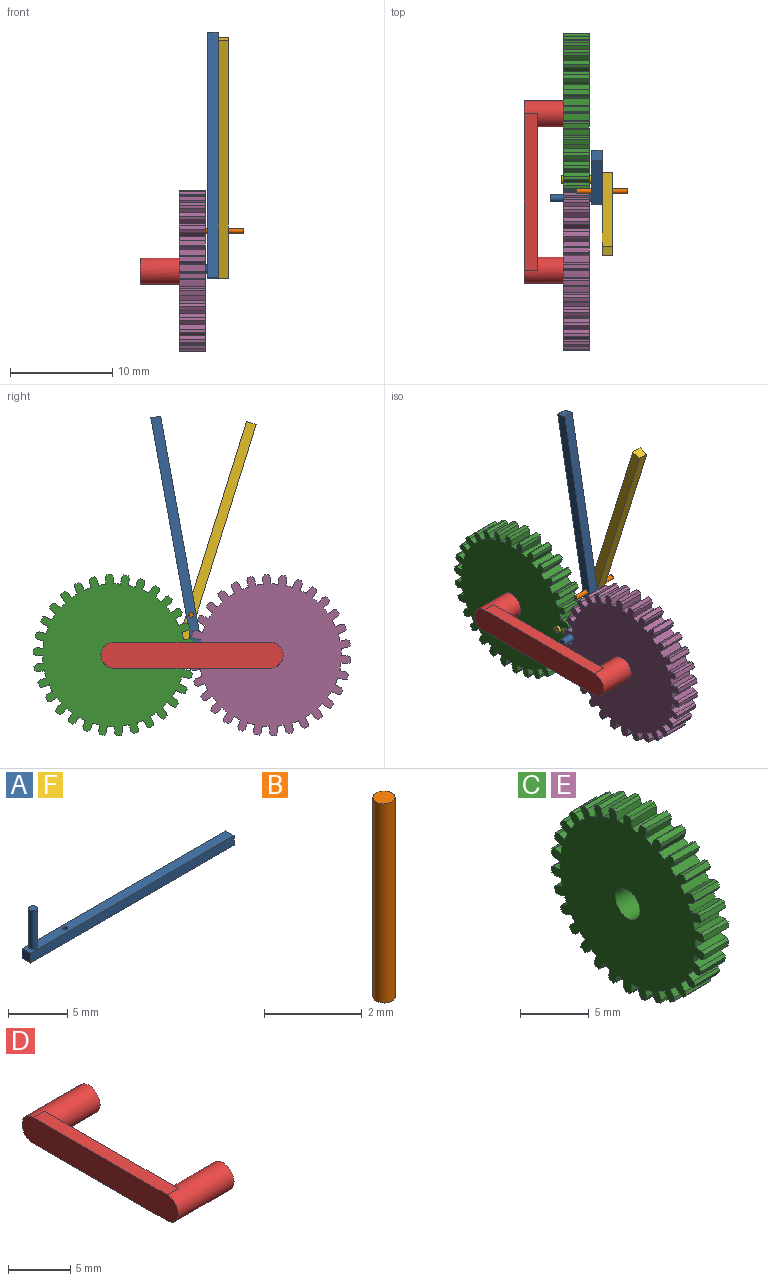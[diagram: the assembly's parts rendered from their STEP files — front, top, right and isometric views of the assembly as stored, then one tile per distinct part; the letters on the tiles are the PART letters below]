
ASSEMBLY  parts=6 mates=4
PART A: 9 faces, bbox 24.3x1x5 mm
  f0: plane 24.3x1mm, normal (0,1,0), area 24.3mm2, adj f1,f4,f5,f6
  f1: plane 1x0.98mm, normal (-1,0,0), area 1mm2, adj f0,f2,f5,f6
  f2: plane 24.3x1mm, normal (0,-1,0), area 24.3mm2, adj f1,f4,f5,f6
  f3: cylinder r=0.23mm len=1mm, axis (0,0,-1), area 1.4mm2, adj f5,f6
  f4: plane 1x0.98mm, normal (1,0,0), area 1mm2, adj f0,f2,f5,f6
  f5: plane 24.3x0.98mm, normal (0,0,1), area 23.3mm2, adj f0,f1,f2,f3,f4,f7
  f6: plane 24.3x0.98mm, normal (0,0,-1), area 23.7mm2, adj f0,f1,f2,f3,f4
  f7: cylinder r=0.36mm len=4mm, axis (0,0,-1), area 9.1mm2, adj f5,f8
  f8: plane 0.73x0.73mm, normal (0,0,1), area 0.4mm2, adj f7
PART B: 3 faces, bbox 0.5x0.5x5 mm
  f0: cylinder r=0.23mm len=5mm, axis (0,0,1), area 7.1mm2, adj f1,f2
  f1: plane 0.45x0.45mm, normal (0,0,-1), area 0.2mm2, adj f0
  f2: plane 0.45x0.45mm, normal (0,0,1), area 0.2mm2, adj f0
PART C: 183 faces, bbox 2.5x15.7x15.8 mm
  f0: cylinder r=6.97mm len=2.54mm, axis (1,0,0), area 1.8mm2, adj f29,f30,f34,f178
  f1: cylinder r=6.97mm len=2.54mm, axis (1,0,0), area 1.8mm2, adj f29,f30,f41,f175
  f2: cylinder r=6.97mm len=2.54mm, axis (1,0,0), area 1.8mm2, adj f29,f30,f46,f170
  f3: cylinder r=6.97mm len=2.54mm, axis (1,0,0), area 1.8mm2, adj f29,f30,f51,f165
  f4: cylinder r=6.97mm len=2.54mm, axis (1,0,0), area 1.8mm2, adj f29,f30,f56,f160
  f5: cylinder r=6.97mm len=2.54mm, axis (1,0,0), area 1.8mm2, adj f29,f30,f61,f155
  f6: cylinder r=6.97mm len=2.54mm, axis (1,0,0), area 1.8mm2, adj f29,f30,f64,f150
  f7: cylinder r=6.97mm len=2.54mm, axis (1,0,0), area 1.8mm2, adj f29,f30,f145,f151
  f8: cylinder r=6.97mm len=2.54mm, axis (1,0,0), area 1.8mm2, adj f29,f30,f140,f146
  f9: cylinder r=6.97mm len=2.54mm, axis (1,0,0), area 1.8mm2, adj f29,f30,f135,f141
  f10: cylinder r=6.97mm len=2.54mm, axis (1,0,0), area 1.8mm2, adj f29,f30,f130,f136
  f11: cylinder r=6.97mm len=2.54mm, axis (1,0,0), area 1.8mm2, adj f29,f30,f125,f131
  f12: cylinder r=6.97mm len=2.54mm, axis (1,0,0), area 1.8mm2, adj f29,f30,f120,f126
  f13: cylinder r=6.97mm len=2.54mm, axis (1,0,0), area 1.8mm2, adj f29,f30,f115,f121
  f14: cylinder r=6.97mm len=2.54mm, axis (1,0,0), area 1.8mm2, adj f29,f30,f110,f116
  f15: cylinder r=6.97mm len=2.54mm, axis (1,0,0), area 1.8mm2, adj f29,f30,f105,f111
  f16: cylinder r=6.97mm len=2.54mm, axis (1,0,0), area 1.8mm2, adj f29,f30,f100,f106
  f17: cylinder r=6.97mm len=2.54mm, axis (1,0,0), area 1.8mm2, adj f29,f30,f95,f101
  f18: cylinder r=6.97mm len=2.54mm, axis (1,0,0), area 1.8mm2, adj f29,f30,f90,f96
  f19: cylinder r=6.97mm len=2.54mm, axis (1,0,0), area 1.8mm2, adj f29,f30,f85,f91
  f20: cylinder r=6.97mm len=2.54mm, axis (1,0,0), area 1.8mm2, adj f29,f30,f80,f86
  f21: cylinder r=6.97mm len=2.54mm, axis (1,0,0), area 1.8mm2, adj f29,f30,f75,f156
  f22: cylinder r=6.97mm len=2.54mm, axis (1,0,0), area 1.8mm2, adj f29,f30,f70,f76
  f23: cylinder r=6.97mm len=2.54mm, axis (1,0,0), area 1.8mm2, adj f29,f30,f65,f71
  f24: cylinder r=6.97mm len=2.54mm, axis (1,0,0), area 1.8mm2, adj f29,f30,f60,f161
  f25: cylinder r=6.97mm len=2.54mm, axis (1,0,0), area 1.8mm2, adj f29,f30,f55,f166
  f26: cylinder r=6.97mm len=2.54mm, axis (1,0,0), area 1.8mm2, adj f29,f30,f50,f171
  f27: cylinder r=6.97mm len=2.54mm, axis (1,0,0), area 1.8mm2, adj f29,f30,f45,f176
  f28: cylinder r=6.97mm len=2.54mm, axis (1,0,0), area 1.8mm2, adj f29,f30,f40,f179
  f29: plane 15.76x15.72mm, normal (1,0,0), area 167.1mm2, adj f0,f1,f2,f3,f4,f5,f6,f7
  f30: plane 15.76x15.72mm, normal (-1,0,0), area 167.1mm2, adj f0,f1,f2,f3,f4,f5,f6,f7
  f31: cylinder r=7.88mm len=2.54mm, axis (-1,0,0), area 1.2mm2, adj f29,f30,f35,f36
  f32: plane 2.54x0.66mm, normal (0,1,0), area 1.7mm2, adj f29,f30,f33,f36
  f33: cylinder r=6.97mm len=2.54mm, axis (1,0,0), area 1.8mm2, adj f29,f30,f32,f81
  f34: plane 2.54x0.66mm, normal (0,-1,0), area 1.7mm2, adj f0,f29,f30,f35
  f35: plane 2.54x0.27mm, normal (0,-0.87,0.48), area 0.8mm2, adj f29,f30,f31,f34
  f36: plane 2.54x0.27mm, normal (0,0.87,0.48), area 0.8mm2, adj f29,f30,f31,f32
  f37: cylinder r=7.88mm len=2.54mm, axis (-1,0,0), area 1.2mm2, adj f29,f30,f38,f39
  f38: plane 2.54x0.24mm, normal (0,0.6,0.8), area 0.8mm2, adj f29,f30,f37,f40
  f39: plane 2.54x0.3mm, normal (0,-1,0.09), area 0.8mm2, adj f29,f30,f37,f41
  f40: plane 2.54x0.6mm, normal (0,0.91,0.41), area 1.7mm2, adj f28,f29,f30,f38
  f41: plane 2.54x0.6mm, normal (0,-0.91,-0.41), area 1.7mm2, adj f1,f29,f30,f39
  f42: cylinder r=7.88mm len=2.54mm, axis (-1,0,0), area 1.2mm2, adj f29,f30,f43,f44
  f43: plane 2.54x0.3mm, normal (0,0.22,0.97), area 0.8mm2, adj f29,f30,f42,f45
  f44: plane 2.54x0.29mm, normal (0,-0.95,-0.33), area 0.8mm2, adj f29,f30,f42,f46
  f45: plane 2.54x0.49mm, normal (0,0.67,0.74), area 1.7mm2, adj f27,f29,f30,f43
  f46: plane 2.54x0.49mm, normal (0,-0.67,-0.74), area 1.7mm2, adj f2,f29,f30,f44
  f47: cylinder r=7.88mm len=2.54mm, axis (-1,0,0), area 1.2mm2, adj f29,f30,f48,f49
  f48: plane 2.54x0.3mm, normal (0,-0.19,0.98), area 0.8mm2, adj f29,f30,f47,f50
  f49: plane 2.54x0.22mm, normal (0,-0.73,-0.68), area 0.8mm2, adj f29,f30,f47,f51
  f50: plane 2.54x0.62mm, normal (0,0.31,0.95), area 1.7mm2, adj f26,f29,f30,f48
  f51: plane 2.54x0.62mm, normal (0,-0.31,-0.95), area 1.7mm2, adj f3,f29,f30,f49
  f52: cylinder r=7.88mm len=2.54mm, axis (-1,0,0), area 1.2mm2, adj f29,f30,f53,f54
  f53: plane 2.54x0.25mm, normal (0,-0.57,0.82), area 0.8mm2, adj f29,f30,f52,f55
  f54: plane 2.54x0.28mm, normal (0,-0.39,-0.92), area 0.8mm2, adj f29,f30,f52,f56
  f55: plane 2.54x0.65mm, normal (0,-0.1,0.99), area 1.7mm2, adj f25,f29,f30,f53
  f56: plane 2.54x0.65mm, normal (0,0.1,-0.99), area 1.7mm2, adj f4,f29,f30,f54
  f57: cylinder r=7.88mm len=2.54mm, axis (-1,0,0), area 1.2mm2, adj f29,f30,f58,f59
  f58: plane 2.54x0.26mm, normal (0,-0.86,0.52), area 0.8mm2, adj f29,f30,f57,f60
  f59: plane 2.54x0.31mm, normal (0,0.02,-1), area 0.8mm2, adj f29,f30,f57,f61
  f60: plane 2.54x0.57mm, normal (0,-0.5,0.87), area 1.7mm2, adj f24,f29,f30,f58
  f61: plane 2.54x0.57mm, normal (0,0.5,-0.87), area 1.7mm2, adj f5,f29,f30,f59
  f62: plane 2.54x0.29mm, normal (0,-0.96,-0.29), area 0.8mm2, adj f29,f30,f65,f66
  f63: plane 2.54x0.23mm, normal (0,0.75,-0.66), area 0.8mm2, adj f29,f30,f64,f66
  f64: plane 2.54x0.64mm, normal (0,0.98,-0.21), area 1.7mm2, adj f6,f29,f30,f63
  f65: plane 2.54x0.64mm, normal (0,-0.98,0.21), area 1.7mm2, adj f23,f29,f30,f62
  f66: cylinder r=7.88mm len=2.54mm, axis (-1,0,0), area 1.2mm2, adj f29,f30,f62,f63
  f67: cylinder r=7.88mm len=2.54mm, axis (-1,0,0), area 1.2mm2, adj f29,f30,f68,f69
  f68: plane 2.54x0.3mm, normal (0,-1,-0.09), area 0.8mm2, adj f29,f30,f67,f70
  f69: plane 2.54x0.24mm, normal (0,0.6,-0.8), area 0.8mm2, adj f29,f30,f67,f71
  f70: plane 2.54x0.6mm, normal (0,-0.91,0.41), area 1.7mm2, adj f22,f29,f30,f68
  f71: plane 2.54x0.6mm, normal (0,0.91,-0.41), area 1.7mm2, adj f23,f29,f30,f69
  f72: cylinder r=7.88mm len=2.54mm, axis (-1,0,0), area 1.2mm2, adj f29,f30,f73,f74
  f73: plane 2.54x0.3mm, normal (0,-0.99,0.12), area 0.8mm2, adj f29,f30,f72,f75
  f74: plane 2.54x0.28mm, normal (0,0.42,-0.91), area 0.8mm2, adj f29,f30,f72,f76
  f75: plane 2.54x0.53mm, normal (0,-0.81,0.59), area 1.7mm2, adj f21,f29,f30,f73
  f76: plane 2.54x0.53mm, normal (0,0.81,-0.59), area 1.7mm2, adj f22,f29,f30,f74
  f77: cylinder r=7.88mm len=2.54mm, axis (-1,0,0), area 1.2mm2, adj f29,f30,f78,f79
  f78: plane 2.54x0.29mm, normal (0,0.96,0.29), area 0.8mm2, adj f29,f30,f77,f80
  f79: plane 2.54x0.23mm, normal (0,-0.75,0.66), area 0.8mm2, adj f29,f30,f77,f81
  f80: plane 2.54x0.64mm, normal (0,0.98,-0.21), area 1.7mm2, adj f20,f29,f30,f78
  f81: plane 2.54x0.64mm, normal (0,-0.98,0.21), area 1.7mm2, adj f29,f30,f33,f79
  f82: cylinder r=7.88mm len=2.54mm, axis (-1,0,0), area 1.2mm2, adj f29,f30,f83,f84
  f83: plane 2.54x0.3mm, normal (0,1,0.09), area 0.8mm2, adj f29,f30,f82,f85
  f84: plane 2.54x0.24mm, normal (0,-0.6,0.8), area 0.8mm2, adj f29,f30,f82,f86
  f85: plane 2.54x0.6mm, normal (0,0.91,-0.41), area 1.7mm2, adj f19,f29,f30,f83
  f86: plane 2.54x0.6mm, normal (0,-0.91,0.41), area 1.7mm2, adj f20,f29,f30,f84
  f87: cylinder r=7.88mm len=2.54mm, axis (-1,0,0), area 1.2mm2, adj f29,f30,f88,f89
  f88: plane 2.54x0.3mm, normal (0,0.99,-0.12), area 0.8mm2, adj f29,f30,f87,f90
  f89: plane 2.54x0.28mm, normal (0,-0.42,0.91), area 0.8mm2, adj f29,f30,f87,f91
  f90: plane 2.54x0.53mm, normal (0,0.81,-0.59), area 1.7mm2, adj f18,f29,f30,f88
  f91: plane 2.54x0.53mm, normal (0,-0.81,0.59), area 1.7mm2, adj f19,f29,f30,f89
  f92: cylinder r=7.88mm len=2.54mm, axis (-1,0,0), area 1.2mm2, adj f29,f30,f93,f94
  f93: plane 2.54x0.29mm, normal (0,0.95,-0.33), area 0.8mm2, adj f29,f30,f92,f95
  f94: plane 2.54x0.3mm, normal (0,-0.22,0.97), area 0.8mm2, adj f29,f30,f92,f96
  f95: plane 2.54x0.49mm, normal (0,0.67,-0.74), area 1.7mm2, adj f17,f29,f30,f93
  f96: plane 2.54x0.49mm, normal (0,-0.67,0.74), area 1.7mm2, adj f18,f29,f30,f94
  f97: cylinder r=7.88mm len=2.54mm, axis (-1,0,0), area 1.2mm2, adj f29,f30,f98,f99
  f98: plane 2.54x0.26mm, normal (0,0.86,-0.52), area 0.8mm2, adj f29,f30,f97,f100
  f99: plane 2.54x0.31mm, normal (0,-0.02,1), area 0.8mm2, adj f29,f30,f97,f101
  f100: plane 2.54x0.57mm, normal (0,0.5,-0.87), area 1.7mm2, adj f16,f29,f30,f98
  f101: plane 2.54x0.57mm, normal (0,-0.5,0.87), area 1.7mm2, adj f17,f29,f30,f99
  f102: cylinder r=7.88mm len=2.54mm, axis (-1,0,0), area 1.2mm2, adj f29,f30,f103,f104
  f103: plane 2.54x0.22mm, normal (0,0.73,-0.68), area 0.8mm2, adj f29,f30,f102,f105
  f104: plane 2.54x0.3mm, normal (0,0.19,0.98), area 0.8mm2, adj f29,f30,f102,f106
  f105: plane 2.54x0.62mm, normal (0,0.31,-0.95), area 1.7mm2, adj f15,f29,f30,f103
  f106: plane 2.54x0.62mm, normal (0,-0.31,0.95), area 1.7mm2, adj f16,f29,f30,f104
  f107: cylinder r=7.88mm len=2.54mm, axis (-1,0,0), area 1.2mm2, adj f29,f30,f108,f109
  f108: plane 2.54x0.25mm, normal (0,0.57,-0.82), area 0.8mm2, adj f29,f30,f107,f110
  f109: plane 2.54x0.28mm, normal (0,0.39,0.92), area 0.8mm2, adj f29,f30,f107,f111
  f110: plane 2.54x0.65mm, normal (0,0.1,-0.99), area 1.7mm2, adj f14,f29,f30,f108
  f111: plane 2.54x0.65mm, normal (0,-0.1,0.99), area 1.7mm2, adj f15,f29,f30,f109
  f112: cylinder r=7.88mm len=2.54mm, axis (-1,0,0), area 1.2mm2, adj f29,f30,f113,f114
  f113: plane 2.54x0.28mm, normal (0,0.39,-0.92), area 0.8mm2, adj f29,f30,f112,f115
  f114: plane 2.54x0.25mm, normal (0,0.57,0.82), area 0.8mm2, adj f29,f30,f112,f116
  f115: plane 2.54x0.65mm, normal (0,-0.1,-0.99), area 1.7mm2, adj f13,f29,f30,f113
  f116: plane 2.54x0.65mm, normal (0,0.1,0.99), area 1.7mm2, adj f14,f29,f30,f114
  f117: cylinder r=7.88mm len=2.54mm, axis (-1,0,0), area 1.2mm2, adj f29,f30,f118,f119
  f118: plane 2.54x0.3mm, normal (0,0.19,-0.98), area 0.8mm2, adj f29,f30,f117,f120
  f119: plane 2.54x0.22mm, normal (0,0.73,0.68), area 0.8mm2, adj f29,f30,f117,f121
  f120: plane 2.54x0.62mm, normal (0,-0.31,-0.95), area 1.7mm2, adj f12,f29,f30,f118
  f121: plane 2.54x0.62mm, normal (0,0.31,0.95), area 1.7mm2, adj f13,f29,f30,f119
  f122: cylinder r=7.88mm len=2.54mm, axis (-1,0,0), area 1.2mm2, adj f29,f30,f123,f124
  f123: plane 2.54x0.31mm, normal (0,-0.02,-1), area 0.8mm2, adj f29,f30,f122,f125
  f124: plane 2.54x0.26mm, normal (0,0.86,0.52), area 0.8mm2, adj f29,f30,f122,f126
  f125: plane 2.54x0.57mm, normal (0,-0.5,-0.87), area 1.7mm2, adj f11,f29,f30,f123
  f126: plane 2.54x0.57mm, normal (0,0.5,0.87), area 1.7mm2, adj f12,f29,f30,f124
  f127: cylinder r=7.88mm len=2.54mm, axis (-1,0,0), area 1.2mm2, adj f29,f30,f128,f129
  f128: plane 2.54x0.3mm, normal (0,-0.22,-0.97), area 0.8mm2, adj f29,f30,f127,f130
  f129: plane 2.54x0.29mm, normal (0,0.95,0.33), area 0.8mm2, adj f29,f30,f127,f131
  f130: plane 2.54x0.49mm, normal (0,-0.67,-0.74), area 1.7mm2, adj f10,f29,f30,f128
  f131: plane 2.54x0.49mm, normal (0,0.67,0.74), area 1.7mm2, adj f11,f29,f30,f129
  f132: cylinder r=7.88mm len=2.54mm, axis (-1,0,0), area 1.2mm2, adj f29,f30,f133,f134
  f133: plane 2.54x0.28mm, normal (0,-0.42,-0.91), area 0.8mm2, adj f29,f30,f132,f135
  f134: plane 2.54x0.3mm, normal (0,0.99,0.12), area 0.8mm2, adj f29,f30,f132,f136
  f135: plane 2.54x0.53mm, normal (0,-0.81,-0.59), area 1.7mm2, adj f9,f29,f30,f133
  f136: plane 2.54x0.53mm, normal (0,0.81,0.59), area 1.7mm2, adj f10,f29,f30,f134
  f137: cylinder r=7.88mm len=2.54mm, axis (-1,0,0), area 1.2mm2, adj f29,f30,f138,f139
  f138: plane 2.54x0.24mm, normal (0,-0.6,-0.8), area 0.8mm2, adj f29,f30,f137,f140
  f139: plane 2.54x0.3mm, normal (0,1,-0.09), area 0.8mm2, adj f29,f30,f137,f141
  f140: plane 2.54x0.6mm, normal (0,-0.91,-0.41), area 1.7mm2, adj f8,f29,f30,f138
  f141: plane 2.54x0.6mm, normal (0,0.91,0.41), area 1.7mm2, adj f9,f29,f30,f139
  f142: cylinder r=7.88mm len=2.54mm, axis (-1,0,0), area 1.2mm2, adj f29,f30,f143,f144
  f143: plane 2.54x0.23mm, normal (0,-0.75,-0.66), area 0.8mm2, adj f29,f30,f142,f145
  f144: plane 2.54x0.29mm, normal (0,0.96,-0.29), area 0.8mm2, adj f29,f30,f142,f146
  f145: plane 2.54x0.64mm, normal (0,-0.98,-0.21), area 1.7mm2, adj f7,f29,f30,f143
  f146: plane 2.54x0.64mm, normal (0,0.98,0.21), area 1.7mm2, adj f8,f29,f30,f144
  f147: cylinder r=7.88mm len=2.54mm, axis (-1,0,0), area 1.2mm2, adj f29,f30,f148,f149
  f148: plane 2.54x0.27mm, normal (0,-0.87,-0.48), area 0.8mm2, adj f29,f30,f147,f150
  f149: plane 2.54x0.27mm, normal (0,0.87,-0.48), area 0.8mm2, adj f29,f30,f147,f151
  f150: plane 2.54x0.66mm, normal (0,-1,0), area 1.7mm2, adj f6,f29,f30,f148
  f151: plane 2.54x0.66mm, normal (0,1,0), area 1.7mm2, adj f7,f29,f30,f149
  f152: cylinder r=7.88mm len=2.54mm, axis (-1,0,0), area 1.2mm2, adj f29,f30,f153,f154
  f153: plane 2.54x0.29mm, normal (0,-0.95,0.33), area 0.8mm2, adj f29,f30,f152,f155
  f154: plane 2.54x0.3mm, normal (0,0.22,-0.97), area 0.8mm2, adj f29,f30,f152,f156
  f155: plane 2.54x0.49mm, normal (0,-0.67,0.74), area 1.7mm2, adj f5,f29,f30,f153
  f156: plane 2.54x0.49mm, normal (0,0.67,-0.74), area 1.7mm2, adj f21,f29,f30,f154
  f157: cylinder r=7.88mm len=2.54mm, axis (-1,0,0), area 1.2mm2, adj f29,f30,f158,f159
  f158: plane 2.54x0.22mm, normal (0,-0.73,0.68), area 0.8mm2, adj f29,f30,f157,f160
  f159: plane 2.54x0.3mm, normal (0,-0.19,-0.98), area 0.8mm2, adj f29,f30,f157,f161
  f160: plane 2.54x0.62mm, normal (0,-0.31,0.95), area 1.7mm2, adj f4,f29,f30,f158
  f161: plane 2.54x0.62mm, normal (0,0.31,-0.95), area 1.7mm2, adj f24,f29,f30,f159
  f162: cylinder r=7.88mm len=2.54mm, axis (-1,0,0), area 1.2mm2, adj f29,f30,f163,f164
  f163: plane 2.54x0.28mm, normal (0,-0.39,0.92), area 0.8mm2, adj f29,f30,f162,f165
  f164: plane 2.54x0.25mm, normal (0,-0.57,-0.82), area 0.8mm2, adj f29,f30,f162,f166
  f165: plane 2.54x0.65mm, normal (0,0.1,0.99), area 1.7mm2, adj f3,f29,f30,f163
  f166: plane 2.54x0.65mm, normal (0,-0.1,-0.99), area 1.7mm2, adj f25,f29,f30,f164
  f167: cylinder r=7.88mm len=2.54mm, axis (-1,0,0), area 1.2mm2, adj f29,f30,f168,f169
  f168: plane 2.54x0.31mm, normal (0,0.02,1), area 0.8mm2, adj f29,f30,f167,f170
  f169: plane 2.54x0.26mm, normal (0,-0.86,-0.52), area 0.8mm2, adj f29,f30,f167,f171
  f170: plane 2.54x0.57mm, normal (0,0.5,0.87), area 1.7mm2, adj f2,f29,f30,f168
  f171: plane 2.54x0.57mm, normal (0,-0.5,-0.87), area 1.7mm2, adj f26,f29,f30,f169
  f172: cylinder r=7.88mm len=2.54mm, axis (-1,0,0), area 1.2mm2, adj f29,f30,f173,f174
  f173: plane 2.54x0.28mm, normal (0,0.42,0.91), area 0.8mm2, adj f29,f30,f172,f175
  f174: plane 2.54x0.3mm, normal (0,-0.99,-0.12), area 0.8mm2, adj f29,f30,f172,f176
  f175: plane 2.54x0.53mm, normal (0,0.81,0.59), area 1.7mm2, adj f1,f29,f30,f173
  f176: plane 2.54x0.53mm, normal (0,-0.81,-0.59), area 1.7mm2, adj f27,f29,f30,f174
  f177: cylinder r=7.88mm len=2.54mm, axis (-1,0,0), area 1.2mm2, adj f29,f30,f180,f181
  f178: plane 2.54x0.64mm, normal (0,0.98,0.21), area 1.7mm2, adj f0,f29,f30,f181
  f179: plane 2.54x0.64mm, normal (0,-0.98,-0.21), area 1.7mm2, adj f28,f29,f30,f180
  f180: plane 2.54x0.29mm, normal (0,-0.96,0.29), area 0.8mm2, adj f29,f30,f177,f179
  f181: plane 2.54x0.23mm, normal (0,0.75,0.66), area 0.8mm2, adj f29,f30,f177,f178
  f182: cylinder r=1.27mm len=2.54mm, axis (1,0,0), area 20.3mm2, adj f29,f30
PART D: 8 faces, bbox 6.4x17.8x2.5 mm
  f0: cylinder r=1.27mm len=6.35mm, axis (1,0,0), area 45.6mm2, adj f1,f2,f4,f5,f6
  f1: plane 2.54x2.54mm, normal (1,0,0), area 5.1mm2, adj f0
  f2: plane 15.24x1.27mm, normal (0,0,1), area 19.4mm2, adj f0,f3,f5,f6
  f3: cylinder r=1.27mm len=6.35mm, axis (1,0,0), area 45.6mm2, adj f2,f4,f5,f6,f7
  f4: plane 15.24x1.27mm, normal (0,0,-1), area 19.4mm2, adj f0,f3,f5,f6
  f5: plane 17.78x2.54mm, normal (-1,0,0), area 43.8mm2, adj f0,f2,f3,f4
  f6: plane 15.24x2.54mm, normal (1,0,0), area 33.6mm2, adj f0,f2,f3,f4
  f7: plane 2.54x2.54mm, normal (1,0,0), area 5.1mm2, adj f3
PART E: same geometry as C
PART F: same geometry as A
PLACE A rot(axis=(-0.09,-0.99,0.09),90.5deg) t=(7.59,1.39,11.29)mm
PLACE B rot(axis=(-0.28,-0.92,0.28),95.1deg) t=(5.09,4.32,10.08)mm fixed
PLACE C rot(axis=(-1,0,0),159.5deg) t=(5.08,7.62,0)mm
PLACE D t=(5.08,-7.62,0)mm
PLACE E rot(axis=(-1,0,0),110.5deg) t=(5.08,-7.62,0)mm
PLACE F rot(axis=(0.15,-0.98,-0.15),91.3deg) t=(8.59,-2.16,11.06)mm
MATE revolute E.f0 <-> D.f0  axis (1,0,0) through (6.35,-7.62,0)mm
MATE revolute C.f0 <-> D.f3  axis (1,0,0) through (6.35,7.62,0)mm
MATE revolute A.f3 <-> B.f0  axis (1,0,0) through (7.59,0.07,3.92)mm
MATE revolute B.f0 <-> F.f3  axis (-1,0,0) through (7.59,0.07,3.92)mm
